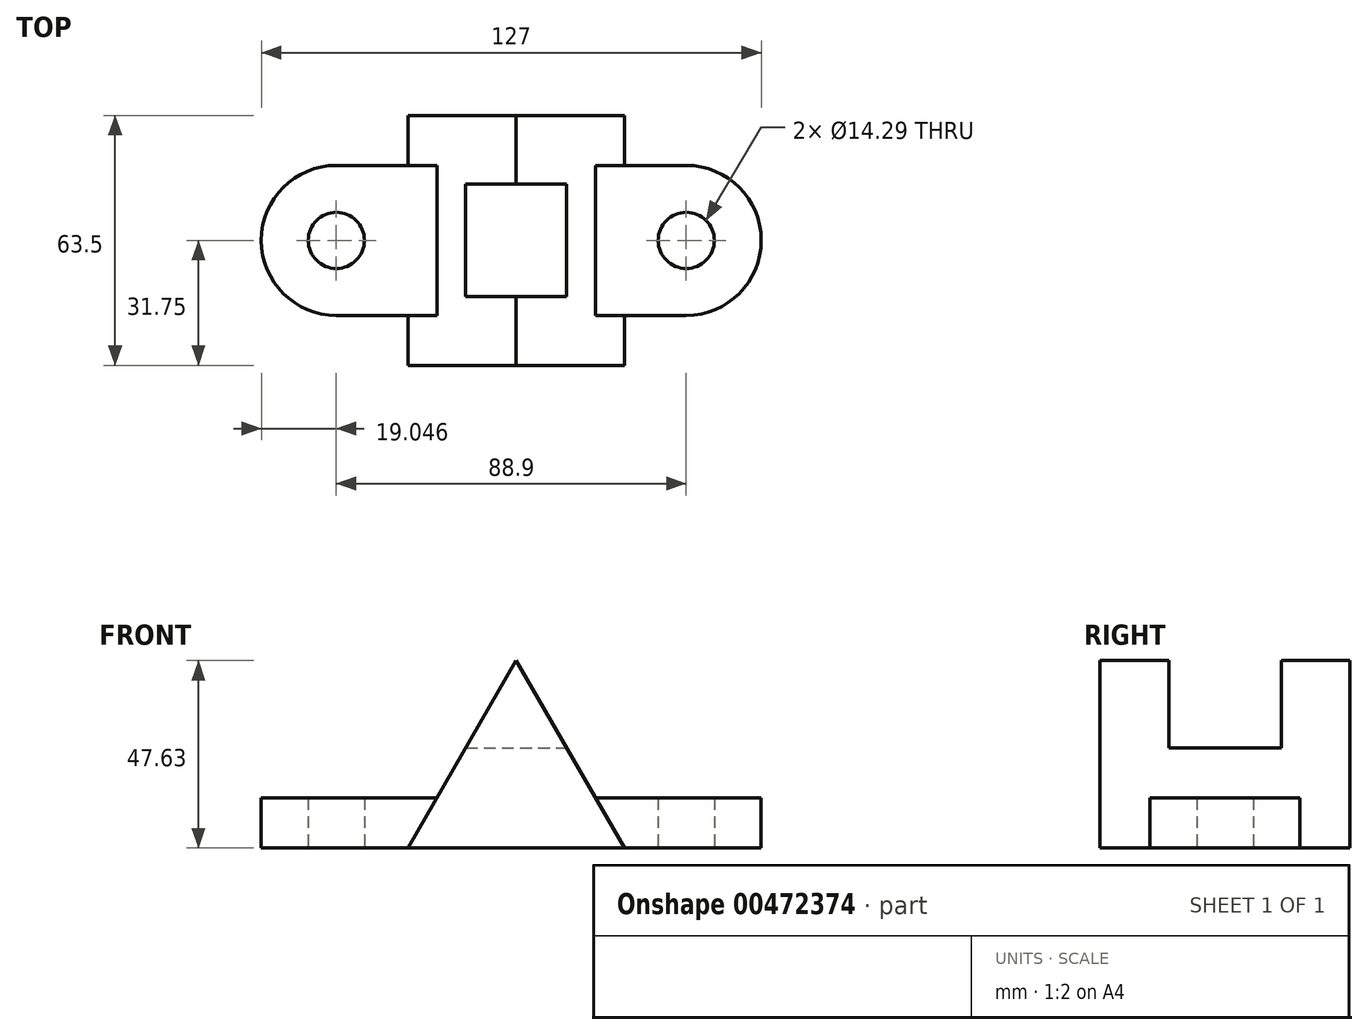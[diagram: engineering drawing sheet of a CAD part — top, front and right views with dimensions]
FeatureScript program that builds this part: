
annotation { "Feature Type Name" : "Feature", "Feature Type Description" : "" }
export const myFeature = defineFeature(function(context is Context, id is Id, definition is map)
    precondition{}
    {
        {
            var Q0;
            Q0=qCreatedBy(makeId("Top.planeOp"),FACE);
            var sketch = newSketch(context, id + "F0", { "sketchPlane" : qUnion([Q0])});
            skLineSegment(sketch, "E0", {"start": v(-45.7, 0) * mm, "end": v(43.2, 0) * mm, "construction": true});
            skArc(sketch, "E1", {"start": v(-45.7, 19.05) * mm, "mid": v(-64.75, 0) * mm, "end": v(-45.7, -19.05) * mm});
            skArc(sketch, "E2", {"start": v(43.2, -19.05) * mm, "mid": v(62.25, 0) * mm, "end": v(43.2, 19.05) * mm});
            skLineSegment(sketch, "E3", {"start": v(-45.7, 19.05) * mm, "end": v(43.2, 19.05) * mm});
            skLineSegment(sketch, "E4", {"start": v(-45.7, -19.05) * mm, "end": v(43.2, -19.05) * mm});
            skCircle(sketch, "E5", {"center": v(-45.7, 0) * mm, "radius": 7.14 * mm});
            skCircle(sketch, "E6", {"center": v(43.2, 0) * mm, "radius": 7.14 * mm});
            skSolve(sketch);
        }
        {
            var Q0;
            Q0 = qSketchRegion(id + "F0", true);
            extrude(context, id + "F1", {"entities" : qUnion([Q0]), "depth" : 12.7 * mm});
        }
        {
            var Q0;
            Q0=qCreatedBy(makeId("Front.planeOp"),FACE);
            var sketch = newSketch(context, id + "F2", { "sketchPlane" : qUnion([Q0])});
            skLineSegment(sketch, "E7", {"start": v(0, 0) * mm, "end": v(0, 47.63) * mm});
            skLineSegment(sketch, "E8", {"start": v(0, 47.63) * mm, "end": v(-27.5, 0) * mm});
            skLineSegment(sketch, "E9", {"start": v(-27.5, 0) * mm, "end": v(27.5, 0) * mm});
            skLineSegment(sketch, "E10", {"start": v(27.5, 0) * mm, "end": v(0, 47.62) * mm});
            skSolve(sketch);
        }
        {
            var Q0;
            Q0 = qSketchRegion(id + "F2", true);
            extrude(context, id + "F3", {"entities" : qUnion([Q0]), "operationType" : NewBodyOperationType.ADD, "depth" : 63.5 * mm, "symmetric" : true});
        }
        {
            var Q0;
            Q0=qCreatedBy(makeId("Right.planeOp"),FACE);
            var sketch = newSketch(context, id + "F4", { "sketchPlane" : qUnion([Q0])});
            skPoint(sketch, "E11", {"position": v(0, 47.63) * mm});
            skLineSegment(sketch, "E12", {"start": v(0, 47.63) * mm, "end": v(-14.29, 47.63) * mm});
            skLineSegment(sketch, "E13", {"start": v(0, 47.63) * mm, "end": v(14.29, 47.63) * mm});
            skLineSegment(sketch, "E14", {"start": v(-14.29, 47.63) * mm, "end": v(-14.29, 25.4) * mm});
            skLineSegment(sketch, "E15", {"start": v(14.29, 47.63) * mm, "end": v(14.29, 25.4) * mm});
            skLineSegment(sketch, "E16", {"start": v(-14.29, 25.4) * mm, "end": v(14.29, 25.4) * mm});
            skSolve(sketch);
        }
        {
            var Q0;
            Q0 = qSketchRegion(id + "F4", true);
            extrude(context, id + "F5", {"entities" : qUnion([Q0]), "operationType" : NewBodyOperationType.REMOVE, "oppositeDirection" : true, "depth" : 50.8 * mm, "symmetric" : true});
        }
    });
